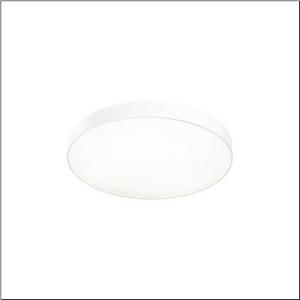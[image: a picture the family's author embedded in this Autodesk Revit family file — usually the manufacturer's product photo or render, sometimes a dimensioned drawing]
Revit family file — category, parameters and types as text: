
# Revit family: round_21_m_51mr36gd0321w
name_source: partatom
category: Lighting Fixtures
units: mm (PartAtom-declared; Revit-internal decimal feet)

## family parameters
Cut with Voids When Loaded = No
Host = Face
Light Source = No
Part Type = Normal
Room Calculation Point = No
Round Connector Dimension = Use Diameter
Shared = No

## types (1)
- Round 21 M (1 x LED, 7550 lm, 54.6 W, 3000K)
    Apparent Load = 55 VA
    CIE Flux Codes = 49 80 96 85 100
    Color Rendering = 80
    Color Temperature = 3000K
    Default Elevation = 1800 mm
    Description = Round 21 M, wall and ceiling luminaire, primary optical cover: cover, of PMMA, opal, light emission: direct/indirect distribution, primary light characteristic: symmetric, installation type: suspended mounting, surface-mounted, LED, rated luminous flux: 7.550lm, luminous efficacy: 138lm/W, light colour: 830, colour temperature: 3000K, control gear: DALI 2, with terminal, 5-pole, mains connection: 230V, AC, 50/60Hz, rated input power: 54.6W, housing, of aluminium, coated, white, diameter: 600mm, height: 62mm, protection rating (complete): IP40, insulation class (complete): insulation class I (protective earthing), certification: CE, impact resistance: IK04, permissible operating ambient temperature: -10..+35°C, packaging unit: 1 piece
    Height = 87 mm
    Lamp = 1 x LED
    Lamp Light Flux = 7550 lm
    Lamp Power = 54.6 W
    Lamp count = 1
    Length = 600 mm
    Luminous efficacy = 138 lm/W
    Manufacturer = Siteco
    ModVariant = No
    Model = 51MR36GD0321W
    Mounting Place = Ceiling
    Mounting Type = Surface mounted
    Number of Poles = 1
    OnlyDefault = Yes
    Power Factor = 1
    Product Name = Round 21 M
    Product group = wall and ceiling luminaire | ceiling mounted
    ProductGroupID = 304
    Protection Class = Protection class I
    Protection Degree = IP 40
    RLX_Detail_Level = 1
    RLX_Emergency_Light_Flux = 0 lm
    RLX_Emergency_Type = 0
    RLX_Emergency_Type_DB = No
    RlxData = <blob elided: 12145 chars, md5=f7647efe>
    Socket = socket
    Standby Power = 0 W
    System Light Flux = 7550 lm
    System Power = 55 W
    Type Comments = Product without accessories
    Type Image = l_1258330.jpg
    URL = http://relux.com
    VarID = ---
    Voltage = 0 V
    Weight = 0.00 kg
    Width = 0 mm  [stored 0 ft]

note: [stored X ft] marks values corroborated as IEEE doubles in the binary element streams (Revit-internal decimal feet)

## geometry (parser evidence)
native form markers: Sweep x12
no freeform markers — native parametric forms only
